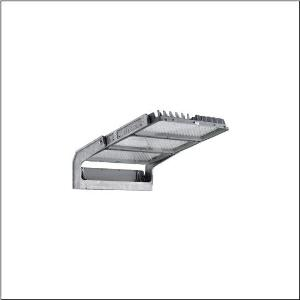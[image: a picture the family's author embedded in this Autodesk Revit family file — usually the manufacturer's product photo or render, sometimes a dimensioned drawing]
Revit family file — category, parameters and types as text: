
# Revit family: floodlight_fl_11_maxi_pro___rs07_5xa779125k01ab_fc8a
name_source: partatom
category: Lighting Fixtures
units: mm (PartAtom-declared; Revit-internal decimal feet)

## family parameters
Cut with Voids When Loaded = No
Host = Face
Light Source = No
Part Type = Normal
Room Calculation Point = No
Round Connector Dimension = Use Diameter
Shared = No

## types (1)
- --- (1 x LED, 179620 lm, 1524.2 W, 3000K)
    Apparent Load = 1524 VA
    CIE Flux Codes = 80 93 99 100 99
    Color Rendering = 70
    Color Temperature = 3000K
    Default Elevation = 1800 mm
    Description = Floodlight FL 11  maxi  pro floodlight; light control with lens of PMMA; cover panel of toughened safety glass, transparent; light distribution: RS07, rotationally symmetric direct distribution, LED; colour temperature: 3000K, rated luminous flux: 179.620lm, colour rendering: CRI > 70, light colour: 730; luminous efficacy: 118lm/W; brightness control: DALI 2; with terminal, 5-pole, max. 2.5mm², mains connection: 220..240V/380..400V AC, 50/60Hz, surge voltage resistance: line to ground: 10kV, LED service life up to 100,000h L90. Typical operating time: 1000h per year., ECG replaceable separately, LED unit replaceable without ESD environment, dustproof LED module, dimming range 10..100%; 1524W floodlight with 3x LED unit of diecast aluminium, coated grey; length: 1.003mm / width: 651mm / height: 338mm; mounting bracket, of diecast aluminium, uncoated, natural, equipment: Power, protection rating (complete): IP66; insulation class (complete): insulation class I (protective earthing); certification: CE, ENEC, VDE; ball protection: ball impact resistant, only for outdoor installations in the designated locations, permissible operating ambient temperature: -40..+55°C, permissible storage temperature: -40..+85°Cpackaging unit: 1 piece

Light Distribution: RS07
    Height = 320 mm
    Lamp = 1 x LED
    Lamp Light Flux = 179620 lm
    Lamp Power = 1524.2 W
    Lamp count = 1
    Length = 1002 mm
    Luminous efficacy = 118 lm/W
    Manufacturer = Siteco
    ModVariant = No
    Model = 5XA779125K01AB
    Mounting Place = Ceiling
    Mounting Type = Surface mounted
    Number of Poles = 1
    OnlyDefault = Yes
    Power Factor = 1
    Product Name = Floodlight FL 11 maxi pro | RS07
    Product group = floodlight | ceiling mounted
    ProductGroupID = 303
    Protection Class = Protection class I
    Protection Degree = IP 66
    RLX_Detail_Level = 1
    RLX_Emergency_Light_Flux = 0 lm
    RLX_Emergency_Type = 0
    RLX_Emergency_Type_DB = No
    RlxData = <blob elided: 40293 chars, md5=2f496281>
    Socket = socket
    Standby Power = 0 W
    System Light Flux = 179620 lm
    System Power = 1524 W
    Type Comments = factory setting: luminous flux: 100 % | dim-lin: 254 | 1030 mA
    Type Image = l_1356210.jpg
    URL = http://relux.com
    VarID = @adj_039095
    Voltage = 0 V
    Weight = 0.00 kg
    Width = 655 mm

## geometry (parser evidence)
native form markers: Blend x4, Sweep x13
no freeform markers — native parametric forms only
